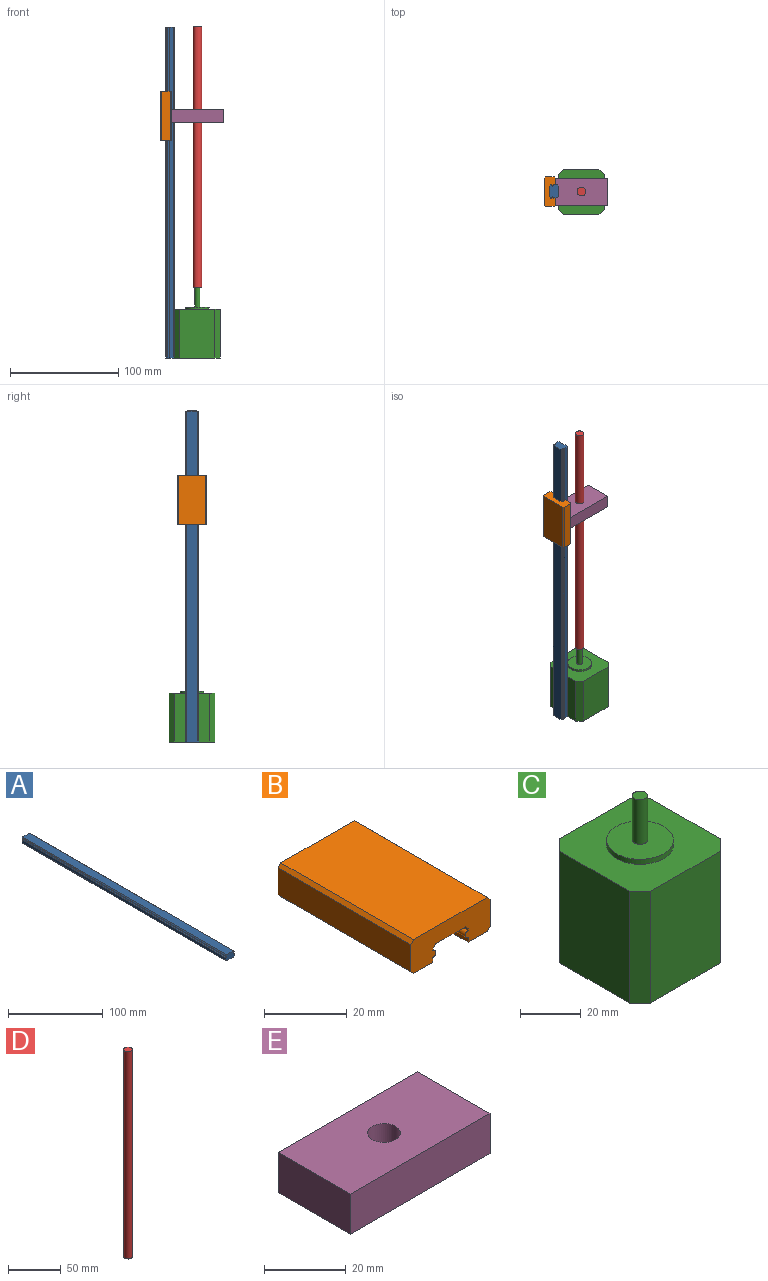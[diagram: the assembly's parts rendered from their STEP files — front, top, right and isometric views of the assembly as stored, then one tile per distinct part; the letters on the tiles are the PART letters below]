
ASSEMBLY  parts=5 mates=3
PART A: 14 faces, bbox 12x304.8x8 mm
  f0: plane 304.8x10mm, normal (0,0,-1), area 3048mm2, adj f1,f11,f12,f13
  f1: plane 304.8x1mm, normal (-0.71,0,-0.71), area 431.1mm2, adj f0,f2,f12,f13
  f2: plane 304.8x3.46mm, normal (-1,0,0), area 1053.9mm2, adj f1,f3,f12,f13
  f3: cylinder r=1mm len=304.8mm, axis (0,1,0), area 957.6mm2, adj f2,f4,f12,f13
  f4: plane 304.8x0.54mm, normal (-1,0,0), area 165.3mm2, adj f3,f5,f12,f13
  f5: plane 304.8x1mm, normal (-0.71,0,0.71), area 431.1mm2, adj f4,f6,f12,f13
  f6: plane 304.8x10mm, normal (0,0,1), area 3048mm2, adj f5,f7,f12,f13
  f7: plane 304.8x1mm, normal (0.71,0,0.71), area 431.1mm2, adj f6,f8,f12,f13
  f8: plane 304.8x0.54mm, normal (1,0,0), area 165.3mm2, adj f7,f9,f12,f13
  f9: cylinder r=1mm len=304.8mm, axis (0,1,0), area 957.6mm2, adj f8,f10,f12,f13
  f10: plane 304.8x3.46mm, normal (1,0,0), area 1053.9mm2, adj f9,f11,f12,f13
  f11: plane 304.8x1mm, normal (0.71,0,-0.71), area 431.1mm2, adj f0,f10,f12,f13
  f12: plane 12x8mm, normal (0,-1,0), area 90.9mm2, adj f0,f1,f2,f3,f4,f5,f6,f7
  f13: plane 12x8mm, normal (0,1,0), area 90.9mm2, adj f0,f1,f2,f3,f4,f5,f6,f7
PART B: 20 faces, bbox 27x45.4x10 mm
  f0: plane 45.4x6.5mm, normal (0,0,-1), area 295.1mm2, adj f1,f6,f12,f18
  f1: plane 27x10mm, normal (0,-1,0), area 212.1mm2, adj f0,f2,f3,f4,f5,f7,f8,f9
  f2: plane 45.4x25mm, normal (0,0,1), area 1135mm2, adj f1,f6,f16,f19
  f3: plane 45.4x8mm, normal (-1,0,0), area 363.2mm2, adj f1,f6,f18,f19
  f4: plane 45.4x6.5mm, normal (0,0,-1), area 295.1mm2, adj f1,f6,f13,f17
  f5: plane 45.4x8mm, normal (1,0,0), area 363.2mm2, adj f1,f6,f16,f17
  f6: plane 27x10mm, normal (0,1,0), area 212.1mm2, adj f0,f2,f3,f4,f5,f7,f8,f9
  f7: cylinder r=1mm len=45.4mm, axis (0,1,0), area 142.6mm2, adj f1,f6,f8,f13
  f8: plane 45.4x0.54mm, normal (-1,0,0), area 24.6mm2, adj f1,f6,f7,f15
  f9: plane 45.4x10mm, normal (0,0,-1), area 454mm2, adj f1,f6,f14,f15
  f10: plane 45.4x0.54mm, normal (1,0,0), area 24.6mm2, adj f1,f6,f11,f14
  f11: cylinder r=1mm len=45.4mm, axis (0,1,0), area 142.6mm2, adj f1,f6,f10,f12
  f12: plane 45.4x1.46mm, normal (1,0,0), area 66.2mm2, adj f0,f1,f6,f11
  f13: plane 45.4x1.46mm, normal (-1,0,0), area 66.2mm2, adj f1,f4,f6,f7
  f14: plane 45.4x1mm, normal (0.71,0,-0.71), area 64.2mm2, adj f1,f6,f9,f10
  f15: plane 45.4x1mm, normal (-0.71,0,-0.71), area 64.2mm2, adj f1,f6,f8,f9
  f16: plane 45.4x1mm, normal (0.71,0,0.71), area 64.2mm2, adj f1,f2,f5,f6
  f17: plane 45.4x1mm, normal (0.71,0,-0.71), area 64.2mm2, adj f1,f4,f5,f6
  f18: plane 45.4x1mm, normal (-0.71,0,-0.71), area 64.2mm2, adj f0,f1,f3,f6
  f19: plane 45.4x1mm, normal (-0.71,0,0.71), area 64.2mm2, adj f1,f2,f3,f6
PART C: 14 faces, bbox 42.3x42.3x65 mm
  f0: plane 45x32.3mm, normal (1,0,0), area 1453.5mm2, adj f4,f5,f10,f12
  f1: plane 45x32.3mm, normal (0,1,0), area 1453.5mm2, adj f4,f5,f12,f13
  f2: plane 45x32.3mm, normal (-1,0,0), area 1453.5mm2, adj f4,f5,f11,f13
  f3: plane 45x32.3mm, normal (0,-1,0), area 1453.5mm2, adj f4,f5,f10,f11
  f4: plane 42.3x42.3mm, normal (0,0,-1), area 1739.3mm2, adj f0,f1,f2,f3,f10,f11,f12,f13
  f5: plane 42.3x42.3mm, normal (0,0,1), area 1359.2mm2, adj f0,f1,f2,f3,f6,f10,f11,f12
  f6: cylinder r=11mm len=22mm, axis (0,0,-1), area 138.2mm2, adj f5,f7
  f7: plane 22x22mm, normal (0,0,1), area 360.5mm2, adj f6,f8
  f8: cylinder r=2.5mm len=18mm, axis (0,0,-1), area 282.7mm2, adj f7,f9
  f9: plane 5x5mm, normal (0,0,1), area 19.6mm2, adj f8
  f10: plane 45x5mm, normal (0.71,-0.71,0), area 318.2mm2, adj f0,f3,f4,f5
  f11: plane 45x5mm, normal (-0.71,-0.71,0), area 318.2mm2, adj f2,f3,f4,f5
  f12: plane 45x5mm, normal (0.71,0.71,0), area 318.2mm2, adj f0,f1,f4,f5
  f13: plane 45x5mm, normal (-0.71,0.71,0), area 318.2mm2, adj f1,f2,f4,f5
PART D: 3 faces, bbox 8x8x241.2 mm
  f0: cylinder r=4mm len=241.15mm, axis (0,0,-1), area 6060.8mm2, adj f1,f2
  f1: plane 8x8mm, normal (0,0,1), area 50.3mm2, adj f0
  f2: plane 8x8mm, normal (0,0,-1), area 50.3mm2, adj f0
PART E: 7 faces, bbox 48.3x25x12 mm
  f0: plane 48.3x12mm, normal (0,-1,0), area 579.6mm2, adj f1,f3,f5,f6
  f1: plane 25x12mm, normal (1,0,0), area 300mm2, adj f0,f2,f5,f6
  f2: plane 48.3x12mm, normal (0,1,0), area 579.6mm2, adj f1,f3,f5,f6
  f3: plane 25x12mm, normal (-1,0,0), area 300mm2, adj f0,f2,f5,f6
  f4: cylinder r=4mm len=12mm, axis (0,0,-1), area 301.6mm2, adj f5,f6
  f5: plane 48.3x25mm, normal (0,0,1), area 1157.2mm2, adj f0,f1,f2,f3,f4
  f6: plane 48.3x25mm, normal (0,0,-1), area 1157.2mm2, adj f0,f1,f2,f3,f4
PLACE A rot(axis=(0.58,-0.58,-0.58),120deg) t=(43.44,-21.7,151.73)mm
PLACE B rot(axis=(-0.58,-0.58,0.58),120deg) t=(43.44,-21.7,47.68)mm
PLACE C rot(axis=(0,0,-1),180deg) t=(68.59,-21.7,-108.07)mm
PLACE D rot(axis=(0,0,-1),180deg) t=(68.59,-21.7,-88.07)mm
PLACE E rot(axis=(0,0,-1),180deg) t=(68.59,-21.7,64.38)mm
MATE fastened A.f0 <-> C.f0  axis (1,0,0) through (47.44,-21.7,-153.07)mm
MATE fastened E.f1 <-> B.f0  axis (-1,0,0) through (44.44,-21.7,70.38)mm
MATE fastened C.f8 <-> D.f0  axis (0,0,1) through (68.59,-21.7,-88.07)mm
